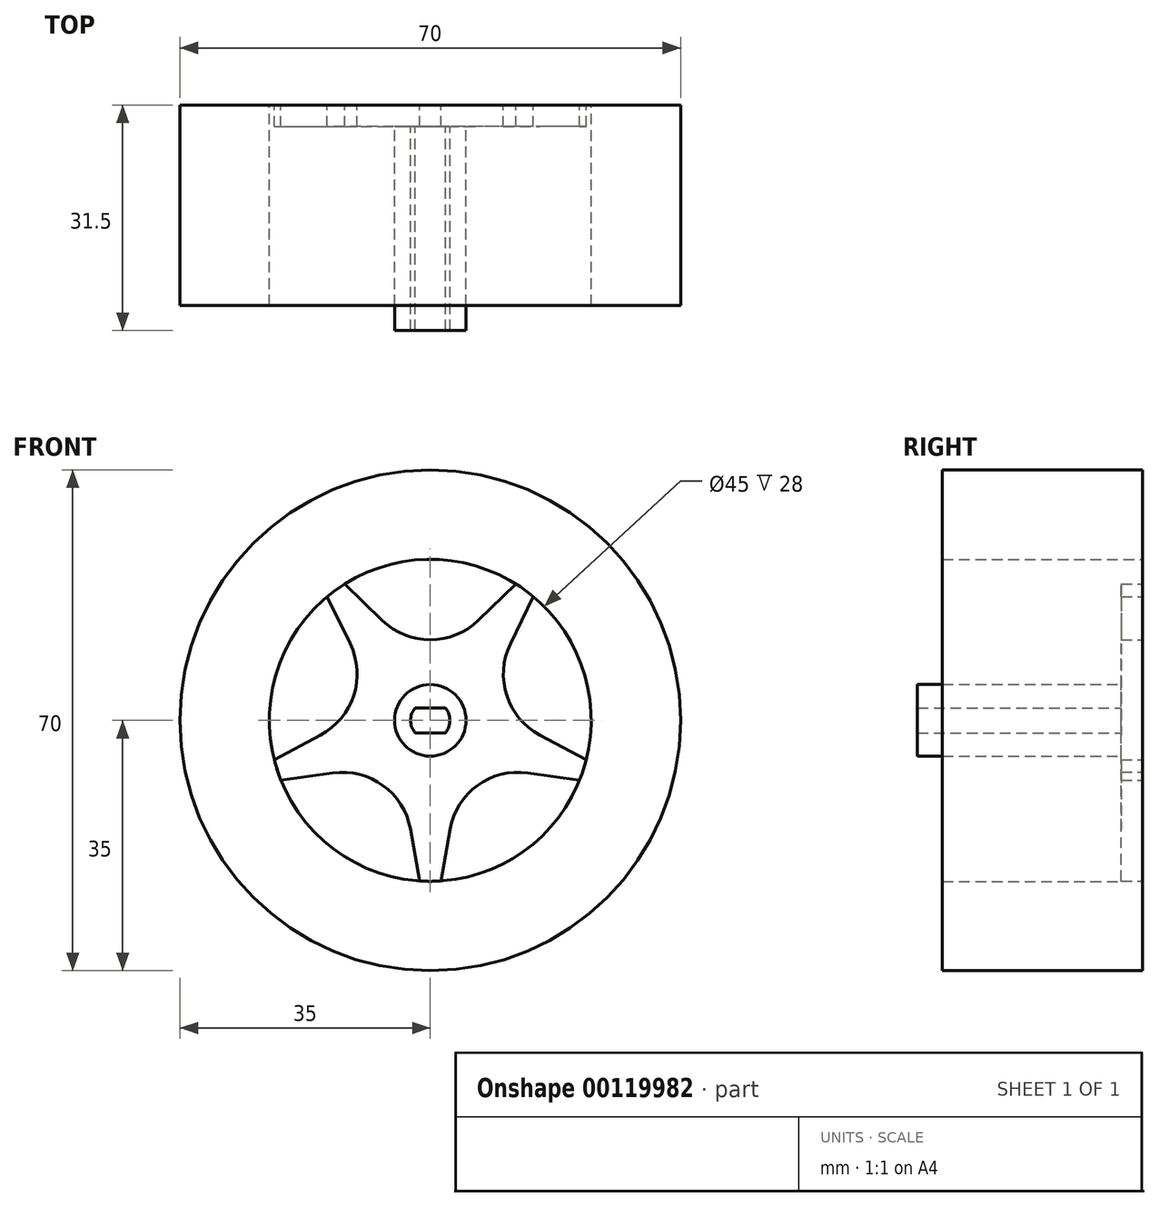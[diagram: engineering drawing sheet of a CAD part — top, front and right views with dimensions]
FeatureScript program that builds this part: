
annotation { "Feature Type Name" : "Feature", "Feature Type Description" : "" }
export const myFeature = defineFeature(function(context is Context, id is Id, definition is map)
    precondition{}
    {
        {
            var Q0;
            Q0=qCreatedBy(makeId("Front.planeOp"),FACE);
            var sketch = newSketch(context, id + "F0", { "sketchPlane" : qUnion([Q0])});
            skCircle(sketch, "E0", {"center": v(0, 0) * mm, "radius": 22.5 * mm});
            skCircle(sketch, "E1.cCircle", {"center": v(0, 0) * mm, "radius": 2.94 * mm, "construction": true});
            skLineSegment(sketch, "E1.0", {"start": v(0, 3.64) * mm, "end": v(3.46, 1.12) * mm});
            skLineSegment(sketch, "E1.1", {"start": v(3.46, 1.12) * mm, "end": v(2.14, -2.94) * mm});
            skLineSegment(sketch, "E1.2", {"start": v(2.14, -2.94) * mm, "end": v(-2.14, -2.94) * mm});
            skLineSegment(sketch, "E1.3", {"start": v(-2.14, -2.94) * mm, "end": v(-3.46, 1.12) * mm});
            skLineSegment(sketch, "E1.4", {"start": v(-3.46, 1.12) * mm, "end": v(0, 3.64) * mm});
            skPoint(sketch, "E1.0.midPoint", {"position": v(1.73, 2.38) * mm});
            skLineSegment(sketch, "E2", {"start": v(-1.73, 2.38) * mm, "end": v(-13.23, 18.2) * mm, "construction": true});
            skLineSegment(sketch, "E3", {"start": v(1.73, 2.38) * mm, "end": v(13.23, 18.2) * mm, "construction": true});
            skLineSegment(sketch, "E4", {"start": v(2.8, -0.9) * mm, "end": v(21.4, -6.95) * mm, "construction": true});
            skLineSegment(sketch, "E5", {"start": v(0, -2.94) * mm, "end": v(0, -22.5) * mm, "construction": true});
            skLineSegment(sketch, "E6", {"start": v(-2.8, -0.9) * mm, "end": v(-21.4, -6.95) * mm, "construction": true});
            skLineSegment(sketch, "E7", {"start": v(-20.89, -8.36) * mm, "end": v(-13.65, -7.35) * mm});
            skLineSegment(sketch, "E8", {"start": v(-1.5, -22.45) * mm, "end": v(-2.77, -15.25) * mm});
            skArc(sketch, "E9", {"start": v(-2.77, -15.25) * mm, "mid": v(-6.61, -9.1) * mm, "end": v(-13.65, -7.35) * mm});
            skCircle(sketch, "E10", {"center": v(0, 0) * mm, "radius": 8.75 * mm});
            skLineSegment(sketch, "E11.1.0", {"start": v(1.5, -22.45) * mm, "end": v(2.77, -15.25) * mm});
            skArc(sketch, "E11.1.1", {"start": v(13.65, -7.35) * mm, "mid": v(6.61, -9.1) * mm, "end": v(2.77, -15.25) * mm});
            skLineSegment(sketch, "E11.1.2", {"start": v(20.89, -8.36) * mm, "end": v(13.65, -7.35) * mm});
            skLineSegment(sketch, "E11.2.0", {"start": v(21.81, -5.51) * mm, "end": v(15.36, -2.08) * mm});
            skArc(sketch, "E11.2.1", {"start": v(11.2, 10.71) * mm, "mid": v(10.7, 3.48) * mm, "end": v(15.36, -2.08) * mm});
            skLineSegment(sketch, "E11.2.2", {"start": v(14.4, 17.28) * mm, "end": v(11.2, 10.71) * mm});
            skLineSegment(sketch, "E11.3.0", {"start": v(11.98, 19.04) * mm, "end": v(6.73, 13.97) * mm});
            skArc(sketch, "E11.3.1", {"start": v(-6.73, 13.97) * mm, "mid": v(0, 11.25) * mm, "end": v(6.73, 13.97) * mm});
            skLineSegment(sketch, "E11.3.2", {"start": v(-11.98, 19.04) * mm, "end": v(-6.73, 13.97) * mm});
            skLineSegment(sketch, "E11.4.0", {"start": v(-14.4, 17.28) * mm, "end": v(-11.2, 10.71) * mm});
            skArc(sketch, "E11.4.1", {"start": v(-15.36, -2.08) * mm, "mid": v(-10.7, 3.48) * mm, "end": v(-11.2, 10.71) * mm});
            skLineSegment(sketch, "E11.4.2", {"start": v(-21.81, -5.51) * mm, "end": v(-15.36, -2.08) * mm});
            skCircle(sketch, "E12", {"center": v(0, 0) * mm, "radius": 35 * mm});
            skSolve(sketch);
        }
        {
            var Q0;
            Q0=makeQuery(id+"F0.imprint","IMPRINT",FACE,{"disambiguationData":[TD([[makeQuery(id+"F0.imprint","IMPRINT",EDGE,{"derivedFrom":sQuery(id+"F0.wireOp",EDGE,"E0")}),1.0]])]});
            var Q1;
            Q1=makeQuery(id+"F0.imprint","IMPRINT",FACE,{"disambiguationData":[TD([[makeQuery(id+"F0.imprint","IMPRINT",EDGE,{"derivedFrom":sQuery(id+"F0.wireOp",EDGE,"E1.0")}),1.0]])]});
            var Q2;
            Q2=makeQuery(id+"F0.imprint","IMPRINT",FACE,{"disambiguationData":[TD([[makeQuery(id+"F0.imprint","IMPRINT",EDGE,{"derivedFrom":sQuery(id+"F0.wireOp",EDGE,"E1.0")}),-1.0]])]});
            extrude(context, id + "F1", {"entities" : qUnion([Q0, Q1, Q2]), "depth" : 3 * mm});
        }
        {
            var Q0;
            Q0 = qSketchRegion(id + "F0", true);
            extrude(context, id + "F2", {"entities" : qUnion([Q0]), "operationType" : NewBodyOperationType.ADD, "depth" : 28 * mm});
        }
        {
            var Q0;
            Q0=makeQuery(id+"F1.opExtrude","CAP_FACE",FACE,{"disambiguationData":[OSD([sQuery(id+"F0.wireOp",EDGE,"E0"),sQuery(id+"F0.wireOp",EDGE,"E7"),sQuery(id+"F0.wireOp",EDGE,"E8"),sQuery(id+"F0.wireOp",EDGE,"E9"),sQuery(id+"F0.wireOp",EDGE,"E11.1.0"),sQuery(id+"F0.wireOp",EDGE,"E11.1.1"),sQuery(id+"F0.wireOp",EDGE,"E11.1.2"),sQuery(id+"F0.wireOp",EDGE,"E11.2.0"),sQuery(id+"F0.wireOp",EDGE,"E11.2.1"),sQuery(id+"F0.wireOp",EDGE,"E11.2.2"),sQuery(id+"F0.wireOp",EDGE,"E11.3.0"),sQuery(id+"F0.wireOp",EDGE,"E11.3.1"),sQuery(id+"F0.wireOp",EDGE,"E11.3.2"),sQuery(id+"F0.wireOp",EDGE,"E11.4.0"),sQuery(id+"F0.wireOp",EDGE,"E11.4.1"),sQuery(id+"F0.wireOp",EDGE,"E11.4.2")])],"isStart":false});
            var sketch = newSketch(context, id + "F3", { "sketchPlane" : qUnion([Q0])});
            skCircle(sketch, "E13", {"center": v(0, 0) * mm, "radius": 5 * mm});
            skCircle(sketch, "E14", {"center": v(0, 0) * mm, "radius": 2.75 * mm});
            skLineSegment(sketch, "E15", {"start": v(-2.12, 1.75) * mm, "end": v(2.12, 1.75) * mm});
            skLineSegment(sketch, "E16", {"start": v(2.12, -1.75) * mm, "end": v(-2.12, -1.75) * mm});
            skSolve(sketch);
        }
        {
            var Q0;
            Q0=makeQuery(id+"F3.imprint","IMPRINT",FACE,{"disambiguationData":[TD([[makeQuery(id+"F3.imprint","IMPRINT",EDGE,{"derivedFrom":sQuery(id+"F3.wireOp",EDGE,"E13")}),1.0]])]});
            var Q1;
            {var subQ0=sQuery(id+"F3.wireOp",EDGE,"E15");Q1=makeQuery(id+"F3.imprint","IMPRINT",FACE,{"disambiguationData":[TD([[makeQuery(id+"F3.imprint","IMPRINT",EDGE,{"derivedFrom":subQ0}),1.0]])]});}
            var Q2;
            {var subQ0=sQuery(id+"F3.wireOp",EDGE,"E16");Q2=makeQuery(id+"F3.imprint","IMPRINT",FACE,{"disambiguationData":[TD([[makeQuery(id+"F3.imprint","IMPRINT",EDGE,{"derivedFrom":subQ0}),1.0]])]});}
            extrude(context, id + "F4", {"entities" : qUnion([Q0, Q1, Q2]), "operationType" : NewBodyOperationType.ADD, "depth" : 28.5 * mm});
        }
    });
